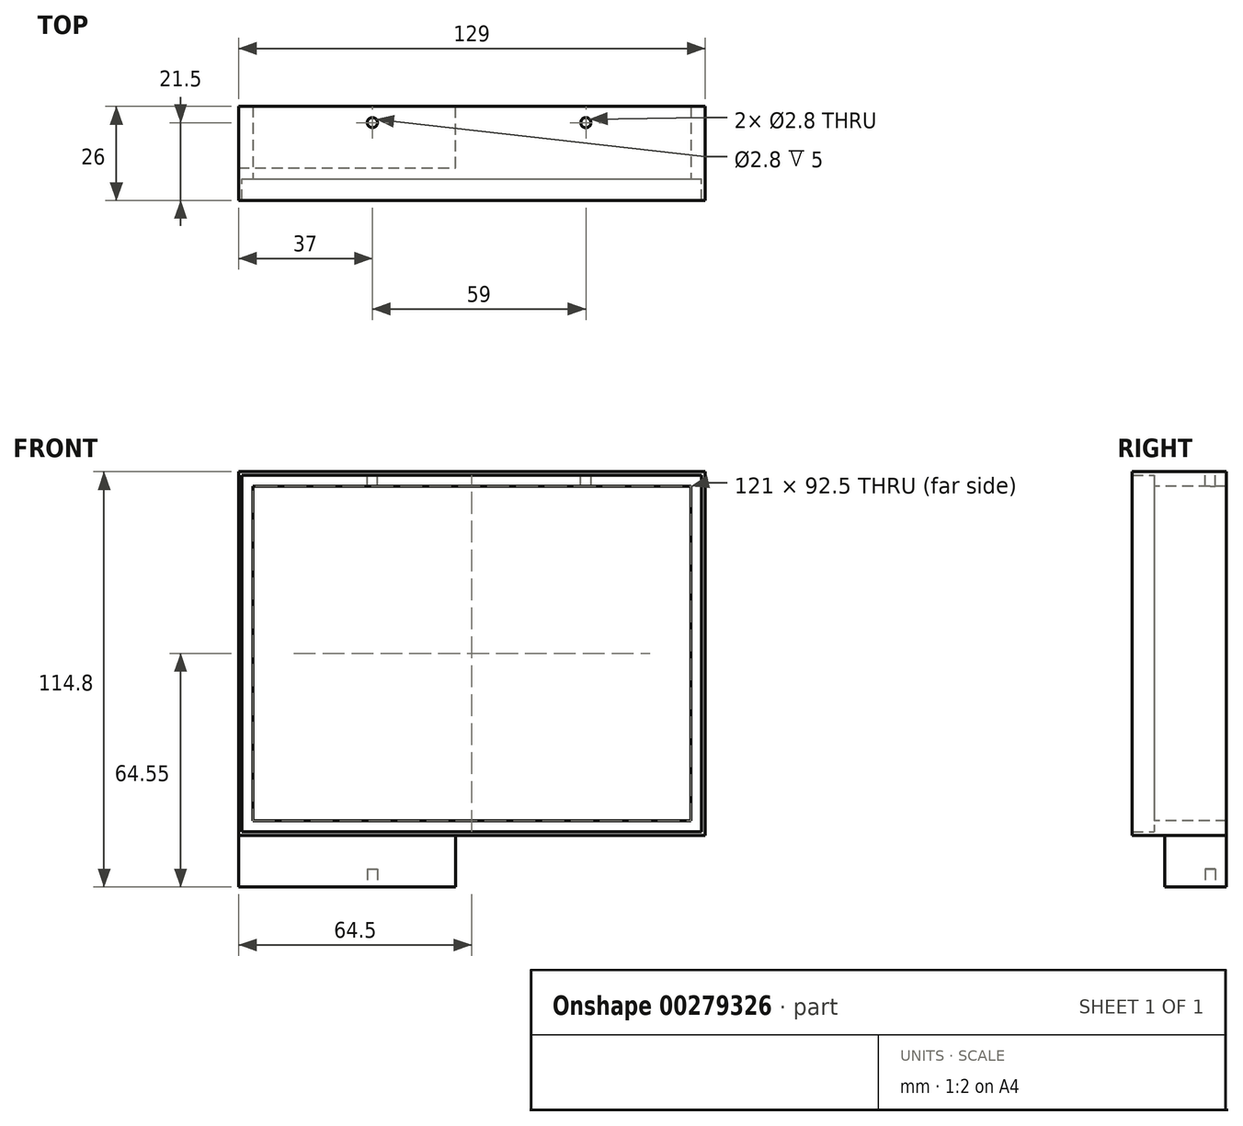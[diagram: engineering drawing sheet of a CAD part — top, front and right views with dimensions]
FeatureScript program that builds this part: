
annotation { "Feature Type Name" : "Feature", "Feature Type Description" : "" }
export const myFeature = defineFeature(function(context is Context, id is Id, definition is map)
    precondition{}
    {
        {
            var Q0;
            Q0=qCreatedBy(makeId("Front.planeOp"),FACE);
            var sketch = newSketch(context, id + "F0", { "sketchPlane" : qUnion([Q0])});
            skLineSegment(sketch, "E0.bottom", {"start": v(57.5, -43) * mm, "end": v(-57.5, -43) * mm});
            skLineSegment(sketch, "E0.top", {"start": v(57.5, 43) * mm, "end": v(-57.5, 43) * mm});
            skLineSegment(sketch, "E0.left", {"start": v(57.5, -43) * mm, "end": v(57.5, 43) * mm});
            skLineSegment(sketch, "E0.right", {"start": v(-57.5, -43) * mm, "end": v(-57.5, 43) * mm});
            skPoint(sketch, "E0.middle", {"position": v(0, 0) * mm});
            skLineSegment(sketch, "E1.bottom", {"start": v(-62.5, 46.5) * mm, "end": v(64.5, 46.5) * mm});
            skLineSegment(sketch, "E1.top", {"start": v(-62.5, -52) * mm, "end": v(64.5, -52) * mm});
            skLineSegment(sketch, "E1.left", {"start": v(-62.5, 46.5) * mm, "end": v(-62.5, -52) * mm});
            skLineSegment(sketch, "E1.right", {"start": v(64.5, 46.5) * mm, "end": v(64.5, -52) * mm});
            skSolve(sketch);
        }
        {
            var Q0;
            Q0=qCreatedBy(makeId("Front.planeOp"),FACE);
            var sketch = newSketch(context, id + "F1", { "sketchPlane" : qUnion([Q0])});
            skLineSegment(sketch, "E2.bottom", {"start": v(-62.5, 46.5) * mm, "end": v(64.5, 46.5) * mm});
            skLineSegment(sketch, "E2.top", {"start": v(-62.5, -52) * mm, "end": v(64.5, -52) * mm});
            skLineSegment(sketch, "E2.left", {"start": v(-62.5, 46.5) * mm, "end": v(-62.5, -52) * mm});
            skLineSegment(sketch, "E2.right", {"start": v(64.5, 46.5) * mm, "end": v(64.5, -52) * mm});
            skLineSegment(sketch, "E3.bottom", {"start": v(-63.5, 47.5) * mm, "end": v(65.5, 47.5) * mm});
            skLineSegment(sketch, "E3.top", {"start": v(-63.5, -53) * mm, "end": v(65.5, -53) * mm});
            skLineSegment(sketch, "E3.left", {"start": v(-63.5, 47.5) * mm, "end": v(-63.5, -53) * mm});
            skLineSegment(sketch, "E3.right", {"start": v(65.5, 47.5) * mm, "end": v(65.5, -53) * mm});
            skSolve(sketch);
        }
        {
            var Q0;
            Q0=qSketchRegion(id+"F1",true);
            extrude(context, id + "F2", {"entities" : qUnion([Q0]), "depth" : 6 * mm});
        }
        {
            var Q0;
            Q0=qCreatedBy(makeId("Front.planeOp"),FACE);
            var sketch = newSketch(context, id + "F3", { "sketchPlane" : qUnion([Q0])});
            skLineSegment(sketch, "E4.bottom", {"start": v(-63.5, 47.5) * mm, "end": v(65.5, 47.5) * mm});
            skLineSegment(sketch, "E4.top", {"start": v(-63.5, -53) * mm, "end": v(65.5, -53) * mm});
            skLineSegment(sketch, "E4.left", {"start": v(-63.5, 47.5) * mm, "end": v(-63.5, -53) * mm});
            skLineSegment(sketch, "E4.right", {"start": v(65.5, 47.5) * mm, "end": v(65.5, -53) * mm});
            skLineSegment(sketch, "E5.bottom", {"start": v(-59.5, 43.5) * mm, "end": v(61.5, 43.5) * mm});
            skLineSegment(sketch, "E5.top", {"start": v(-59.5, -49) * mm, "end": v(61.5, -49) * mm});
            skLineSegment(sketch, "E5.left", {"start": v(-59.5, 43.5) * mm, "end": v(-59.5, -49) * mm});
            skLineSegment(sketch, "E5.right", {"start": v(61.5, 43.5) * mm, "end": v(61.5, -49) * mm});
            skSolve(sketch);
        }
        {
            var Q0;
            Q0=qSketchRegion(id+"F3",true);
            extrude(context, id + "F4", {"entities" : qUnion([Q0]), "operationType" : NewBodyOperationType.ADD, "oppositeDirection" : true, "depth" : 20 * mm});
        }
        {
            var Q0;
            Q0=makeQuery(id+"F4.opExtrude","CAP_FACE",FACE,{"disambiguationData":[OSD([sQuery(id+"F3.wireOp",EDGE,"E4.bottom"),sQuery(id+"F3.wireOp",EDGE,"E4.top"),sQuery(id+"F3.wireOp",EDGE,"E4.left"),sQuery(id+"F3.wireOp",EDGE,"E4.right"),sQuery(id+"F3.wireOp",EDGE,"E5.bottom"),sQuery(id+"F3.wireOp",EDGE,"E5.top"),sQuery(id+"F3.wireOp",EDGE,"E5.left"),sQuery(id+"F3.wireOp",EDGE,"E5.right")])],"isStart":false});
            var sketch = newSketch(context, id + "F5", { "sketchPlane" : qUnion([Q0])});
            skLineSegment(sketch, "E6.top", {"start": v(63.5, -67.3) * mm, "end": v(3.5, -67.3) * mm});
            skLineSegment(sketch, "E6.left", {"start": v(63.5, -53) * mm, "end": v(63.5, -67.3) * mm});
            skLineSegment(sketch, "E6.right", {"start": v(3.5, -53) * mm, "end": v(3.5, -67.3) * mm});
            skLineSegment(sketch, "E7", {"start": v(63.5, -53) * mm, "end": v(3.5, -53) * mm});
            skSolve(sketch);
        }
        {
            var Q0;
            Q0=qSketchRegion(id+"F5",true);
            extrude(context, id + "F6", {"entities" : qUnion([Q0]), "operationType" : NewBodyOperationType.ADD, "oppositeDirection" : true, "depth" : 17 * mm});
        }
        {
            var Q0;
            Q0=makeQuery(id+"F4.boolean.opBoolean","MERGE",FACE,{"derivedFrom":[makeQuery(id+"F2.opExtrude","SWEPT_FACE",FACE,{"disambiguationData":[OSD([sQuery(id+"F1.wireOp",EDGE,"E3.bottom")])]}),makeQuery(id+"F4.opExtrude","SWEPT_FACE",FACE,{"disambiguationData":[OSD([sQuery(id+"F3.wireOp",EDGE,"E4.bottom")])]})]});
            var sketch = newSketch(context, id + "F7", { "sketchPlane" : qUnion([Q0])});
            skCircle(sketch, "E8", {"center": v(-26.5, 15.5) * mm, "radius": 1.4 * mm});
            skCircle(sketch, "E9", {"center": v(32.5, 15.5) * mm, "radius": 1.4 * mm});
            skSolve(sketch);
        }
        {
            var Q0;
            Q0=qSketchRegion(id+"F7",true);
            extrude(context, id + "F8", {"entities" : qUnion([Q0]), "operationType" : NewBodyOperationType.REMOVE, "oppositeDirection" : true, "depth" : 7.9 * mm});
        }
        {
            var Q0;
            Q0=makeQuery(id+"F6.opExtrude","SWEPT_FACE",FACE,{"disambiguationData":[OSD([sQuery(id+"F5.wireOp",EDGE,"E6.top")])]});
            var sketch = newSketch(context, id + "F9", { "sketchPlane" : qUnion([Q0])});
            skCircle(sketch, "E10", {"center": v(-26.5, -15.5) * mm, "radius": 1.4 * mm});
            skSolve(sketch);
        }
        {
            var Q0;
            Q0=qSketchRegion(id+"F9",true);
            extrude(context, id + "F10", {"entities" : qUnion([Q0]), "operationType" : NewBodyOperationType.REMOVE, "oppositeDirection" : true, "depth" : 5 * mm});
        }
    });
